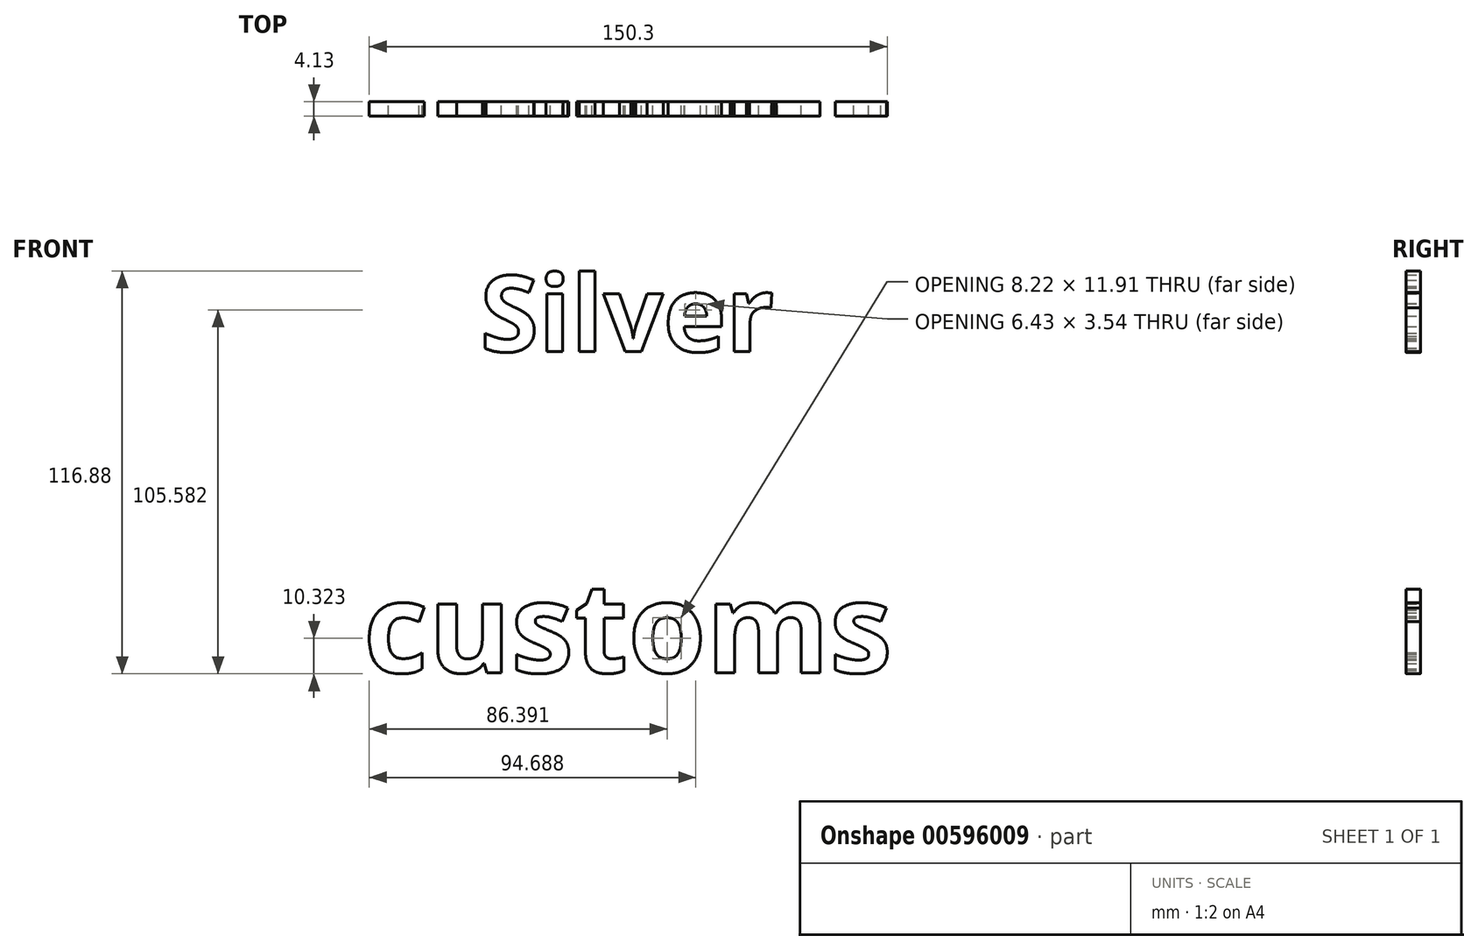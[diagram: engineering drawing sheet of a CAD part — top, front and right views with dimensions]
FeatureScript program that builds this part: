
annotation { "Feature Type Name" : "Feature", "Feature Type Description" : "" }
export const myFeature = defineFeature(function(context is Context, id is Id, definition is map)
    precondition{}
    {
        {
            var Q0;
            Q0=qCreatedBy(makeId("Front.planeOp"),FACE);
            var sketch = newSketch(context, id + "F0", { "sketchPlane" : qUnion([Q0])});
            skText(sketch, "E0", { "text": "Silver", "fontName": "OpenSans-Bold.ttf"});
            skText(sketch, "E1", { "text": "customs", "fontName": "OpenSans-Bold.ttf"});
            const initialGuessF0  = {"E0": [-0.04335, 0.03715, 1, 0, 0.02214], "E1": [-0.07714, -0.056, 1, 0, 0.02628]};
            skSetInitialGuess(sketch, initialGuessF0);
            skSolve(sketch);
        }
        {
            var Q0;
            Q0 = qSketchRegion(id + "F0", true);
            extrude(context, id + "F1", {"entities" : qUnion([Q0]), "depth" : 4.13 * mm, "offsetDistance" : 25.4 * mm});
        }
    });
